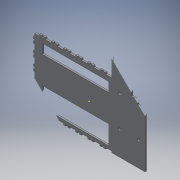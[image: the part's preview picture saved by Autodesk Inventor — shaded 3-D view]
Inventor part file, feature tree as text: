
AUTODESK INVENTOR PART (.ipt)
format: ipt  version: 2016 (Build 200138000, 138)  size: 422,912 bytes
history: native  units: in
note: dims shown in document units (in); Inventor stores cm internally (conversion verified against a paired STEP export)
features: sketch x22, extrude x20, pattern_linear x2, mirror x1, projected_geometry x1
ambient origin geometry x8: Origin, YZ Plane, XZ Plane, XY Plane, X Axis, Y Axis, Z Axis, Center Point
bodies: Solid1 (feature_tree)
feature tree (46):
  extrude  "Extrusion1"  Depth=5.5118in
  extrude  "Extrusion2"  Depth=0.125in
  extrude  "Extrusion3"  Depth=0.2165in
  extrude  "Extrusion4"  Depth=1.5748in
  pattern_linear  "Rectangular Pattern1"  Count1=4  [1 undecoded]
  extrude  "Extrusion5"  Depth=0.5315in
  extrude  "Extrusion6"  Depth=0.2165in
  extrude  "Extrusion7"  Depth=1.5748in
  extrude  "Extrusion8"  Depth=0.5in
  extrude  "Extrusion9"  Depth=0.25in TaperAngle=0.0deg
  extrude  "Extrusion10"  Depth=0.125in
  extrude  "Extrusion11"  Depth=0.25in TaperAngle=0.0deg
  extrude  "Extrusion12"  Depth=1.0in
  pattern_linear  "Rectangular Pattern2"  Count1=10  [1 undecoded]
  extrude  "Extrusion13"  Depth=0.5906in
  sketch  "Sketch14"  dims[d34=0.3937in d35=0.0in d36=0.126in]
  sketch  "Sketch15"  dims[d37=0.1988in d38=0.0394in]
  extrude  "Extrusion14"  Depth=0.3937in
  extrude  "Extrusion15"  Depth=0.0394in
  extrude  "Extrusion16"  Depth=0.0394in
  mirror  "Mirror1"
  extrude  "Extrusion17"  Depth=0.126in
  extrude  "Extrusion18"  Depth=0.1988in
  extrude  "Extrusion19"  Depth=0.0394in
  extrude  "Extrusion20"  Depth=0.3937in TaperAngle=0.0deg
  sketch  "Sketch1"  dims[d0=9.2638in d1=5.5118in]
  sketch  "Sketch2"  dims[d2=0.125in d3=0.0in d4=0.9252in]
  sketch  "Sketch3"  dims[d5=0.5315in d6=0.2165in]
  sketch  "Sketch4"  dims[d7=0.2165in d8=0.9252in d9=1.5748in]
  sketch  "Sketch5"  dims[d10=0.2165in d11=0.5315in]
  sketch  "Sketch6"  dims[d12=2.5591in d13=0.2165in]
  sketch  "Sketch7"  dims[d14=1.5748in d15=2.5591in]
  sketch  "Sketch8"  dims[d16=0.25in d17=0.0in d18=0.5in]
  sketch  "Sketch9"  dims[d19=0.125in d20=0.25in d21=0.0in]
  projected_geometry  "Projected Loop1"
  sketch  "Sketch10"  dims[d22=0.14in d23=0.125in]
  sketch  "Sketch11"  dims[d24=0.18in d25=0.25in d26=0.0in]
  sketch  "Sketch12"  dims[d27=2.3622in d29=1.0in d30=6.4567in d31=3.937in]
  sketch  "Sketch13"  dims[d32=0.5906in d33=1.378in]
  sketch  "Sketch16"  dims[d39=0.126in d40=0.0394in]
  sketch  "Sketch17"  dims[d41=0.1988in d42=0.126in]
  sketch  "Sketch18"  dims[d43=0.0394in d44=0.1988in]
  sketch  "Sketch19"  dims[d45=0.126in d46=0.0394in]
  sketch  "Sketch20"  dims[d47=0.1988in d48=0.3937in d49=0.0in]
  sketch  "Sketch21"  dims[d50=0.25in]
  sketch  "Sketch22"  dims[d51=0.5in d52=0.5in d53=0.3937in d54=0.0in d55=0.14in d56=0.18in d57=0.1in d58=0.3937in d59=0.0in d60=0.1094in d61=0.3125in d63=0.3937in d64=0.0in d65=0.0863in d66=0.0863in d67=0.0in d68=0.6in d69=0.3937in d70=0.0in d71=0.125in d72=0.5in d73=0.3937in d74=0.0in d75=0.138in d76=0.125in d77=0.181in d78=0.3937in d79=0.0in d80=1.9685in d82=1.0in d83=0.25in d84=0.181in d85=0.3937in d86=0.0in d87=0.5906in d88=0.5512in d89=0.3937in d90=0.0in d91=0.125in d92=0.181in d93=0.3937in d94=0.0in d95=0.125in d96=0.5in d97=0.18in d98=0.3937in d99=0.0in d100=1.5748in d101=5.5118in d102=0.25in d103=0.25in d104=0.3937in d105=0.0in d107=1.5748in d108=0.125in d109=0.0in d110=0.2756in d111=0.7874in d112=0.2756in d113=0.5512in d115=0.125in d116=0.0in d117=0.7874in d118=0.3937in d119=0.125in d120=0.0in d121=2.7598in d122=0.922in]
note: 2 required parameter values undecoded (feature->parameter linkage not recoverable at this tier; creation-order binding heuristic only, values carry confidence <= 0.55)
